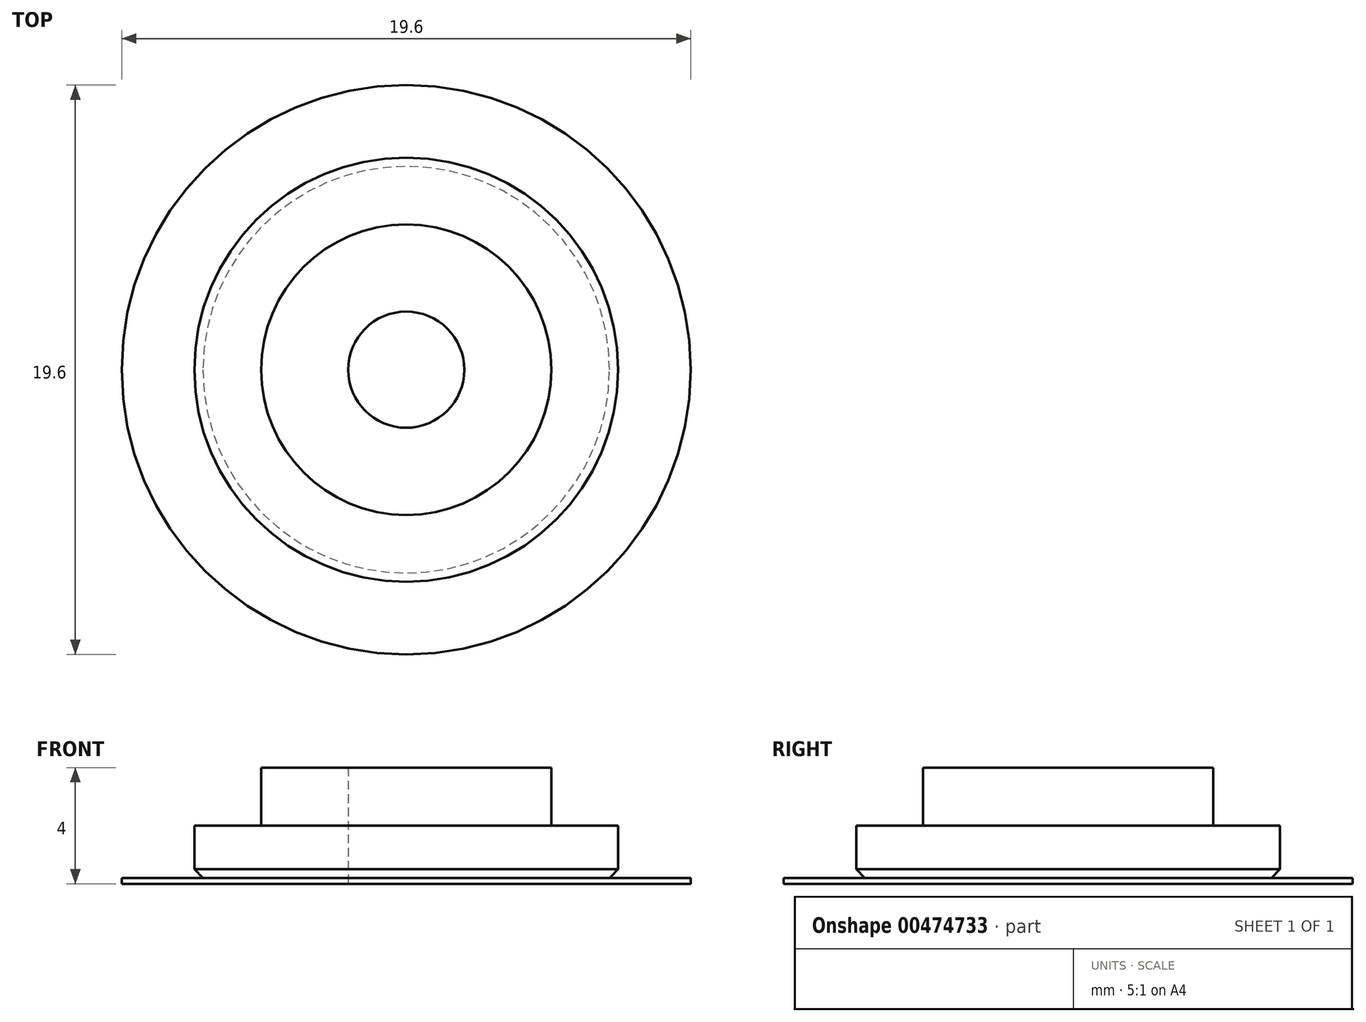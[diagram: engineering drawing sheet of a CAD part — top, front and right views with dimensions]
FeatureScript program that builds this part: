
annotation { "Feature Type Name" : "Feature", "Feature Type Description" : "" }
export const myFeature = defineFeature(function(context is Context, id is Id, definition is map)
    precondition{}
    {
        {
            var Q0;
            Q0=qCreatedBy(makeId("Top.planeOp"),FACE);
            var sketch = newSketch(context, id + "F0", { "sketchPlane" : qUnion([Q0])});
            skCircle(sketch, "E0", {"center": v(0, 0) * mm, "radius": 7.3 * mm});
            skSolve(sketch);
        }
        {
            var Q0;
            Q0=qSketchRegion(id+"F0",true);
            extrude(context, id + "F1", {"entities" : qUnion([Q0]), "depth" : 2 * mm, "offsetDistance" : 25 * mm});
        }
        {
            var Q0;
            Q0=makeQuery(id+"F1.opExtrude","CAP_FACE",FACE,{"disambiguationData":[OSD([sQuery(id+"F0.wireOp",EDGE,"E0")])],"isStart":false});
            var sketch = newSketch(context, id + "F2", { "sketchPlane" : qUnion([Q0])});
            skCircle(sketch, "E1", {"center": v(0, 0) * mm, "radius": 5 * mm});
            skSolve(sketch);
        }
        {
            var Q0;
            Q0=qSketchRegion(id+"F2",true);
            extrude(context, id + "F3", {"entities" : qUnion([Q0]), "operationType" : NewBodyOperationType.ADD, "depth" : 2 * mm, "offsetDistance" : 25 * mm});
        }
        {
            var Q0;
            Q0=makeQuery(id+"F1.opExtrude","CAP_EDGE",EDGE,{"disambiguationData":[OSD([sQuery(id+"F0.wireOp",EDGE,"E0")])],"isStart":true});
            chamfer(context, id + "F4", {"entities" : qUnion([Q0]), "width" : 0.5 * mm, "tangentPropagation" : true});
        }
        {
            var Q0;
            Q0=makeQuery(id+"F1.opExtrude","CAP_FACE",FACE,{"disambiguationData":[OSD([sQuery(id+"F0.wireOp",EDGE,"E0")])],"isStart":true});
            var sketch = newSketch(context, id + "F5", { "sketchPlane" : qUnion([Q0])});
            skCircle(sketch, "E2", {"center": v(0, 0) * mm, "radius": 2 * mm});
            skSolve(sketch);
        }
        {
            var Q0;
            Q0=qSketchRegion(id+"F5",true);
            extrude(context, id + "F6", {"entities" : qUnion([Q0]), "operationType" : NewBodyOperationType.REMOVE, "endBound" : BoundingType.THROUGH_ALL, "oppositeDirection" : true, "depth" : 25 * mm, "offsetDistance" : 25 * mm});
        }
        {
            var Q0;
            Q0=makeQuery(id+"F1.opExtrude","CAP_FACE",FACE,{"disambiguationData":[OSD([sQuery(id+"F0.wireOp",EDGE,"E0")])],"isStart":true});
            var sketch = newSketch(context, id + "F7", { "sketchPlane" : qUnion([Q0])});
            skCircle(sketch, "E3", {"center": v(0, 0) * mm, "radius": 9.8 * mm});
            skCircle(sketch, "E4", {"center": v(0, 0) * mm, "radius": 6.8 * mm});
            skSolve(sketch);
        }
        {
            var Q0;
            Q0 = qSketchRegion(id + "F7", true);
            extrude(context, id + "F8", {"entities" : qUnion([Q0]), "operationType" : NewBodyOperationType.ADD, "oppositeDirection" : true, "depth" : 0.2 * mm, "offsetDistance" : 25 * mm});
        }
    });
